# Revit family: IS_Mara_A9041_BIM_IT
name_source: partatom
category: Plumbing Fixtures
revit_build: Autodesk Revit MEP 2016 (Build: 20161004_0715(x64)
units: mm (PartAtom-declared; Revit-internal decimal feet)

## family parameters
Always vertical = No
Cut with Voids When Loaded = No
OmniClass Number = 23.45.55.17
OmniClass Title = Mixing Faucets
Part Type = Normal
Room Calculation Point = No
Round Connector Dimension = Use Diameter
Shared = No
Work Plane-Based = No

## types (1)
- A9041AA - MARA MISC LVB C/LIM PORTATA BOCCA 120 CR
    Accessori = www.idealstandard.it
    AltezzaNominale = 169 mm  [stored 0.554462 ft]
    Assembly Code = C1030200
    Autore = Ideal Standard Italia
    BIMobject category = Taps & Mixers
    BOSUseNativeGeometries = 1
    Brand = Ideal Standard
    Brand url = http://www.idealstandard.co.uk
    Caratteristiche = Miscelatore monocomando lavabo, con bocca di erogazione fissa da 120 mm. È dotato di cartuccia da 35 mm con limitatore della temperatura e riduttore di portata a 5 l/min. Sistema di fissaggio Easy Fix. Sporgenza bocca 120 mm, altezza bocca 65 mm. Con asta di comando e piletta in metallo cromato da 1-1/4”. Tubi flessibili.
    CodiceABarre = 3800861033394
    Colore = Cromato
    Connessione = Installazione
    CostoDiSostituzione = 0 $
    Description = MARA - Miscelatore monocomando lavabo, con bocca di erogazione fissa da 120 mm. È dotato di cartuccia da 35 mm con limitatore della temperatura e riduttore di portata a 5 l/min. Sistema di fissaggio Easy Fix. Sporgenza bocca 120 mm, altezza bocca 65 mm. Con asta di comando e piletta in metallo cromato da 1-1/4”. Tubi flessibili.
    DescrizioneClassifcazioneUni2015 = Washbasin taps ?
    Dimensione = 169 x 50 x 157
    DurataGaranziaProdotti = 5
    EAN code = https://3800861033394
    Edition number = 1
    Finitura = Cromato
    Garanzia = Garanzia Idealstandard
    IFC Classification = Sanitary Terminal
    InformazioniDiProdotto = www.idealstandard.it/prodotti/html
    InformazioniGaranzia = www.idealstandard.it/garanzia.html
    Installation instructions = www.idealstandard.it/prodotti/html
    InstruzioniInstallazione = www.idealstandard.it/prodotti/html
    LarghezzaNominale = 50 mm  [stored 0.164042 ft]
    LunghezzaNominale = 157 mm
    Manufacturer = www.idealstandard.it
    Manufacturer name = Ideal Standard
    Material main = Brass
    Materiale = Ottone
    Model = A9041AA
    NBS Reference Code = 35-79-95
    NBS Reference Description = Wash Basin And Trough Water Supply Fittings
    Nominal height = 169
    Nominal width = 50
    NumeroDiModello = A9041AA
    OmniClass Code = 23-31 11 00
    OmniClass Description = Faucets
    PesoNetto = 1,418 KG
    Product Guid = fabe5e2e-1783-4b92-abe1-92f1cb9e871c
    Product SKU = A9041
    Product certification = http://www.idealstandard.it
    Product data url = https://bimobject.com
    Product family = MARA
    Product group = Basin Mixer
    Product name = MARA BASIN MIXER RIM GRANDE 5L/MIN PU/M. SPX
    Product url = http://www.idealstandard.it
    QR code = http://bimobject.com
    Revisione = 1
    RiferimentoClassificazioneUni2015 = Pr_40_20_87_98
    Spazio = Interno
    Technical description = www.idealstandard.it/prodotti/html
    Telefono = 800 652 290
    URL = www.idealstandard.it
    Uniclass 1.4 Code = L8212
    Uniclass 1.4 Description = Fittings
    Uniclass 2.0 Code = PR-35-79-95
    Uniclass 2.0 Description = Wash Basin And Trough Water Supply Fittings
    Uniclass 2015 Code = Pr_40_20_87_96
    Uniclass 2015 Name = Washbasin manual water supply sets
    UnitaDurata = anni
    UnitaDurataGaranzia = anni
    UnitaLineare = milimetri
    UnitaVolume = Litri
    Versione = 1
    VersioneClassificazioneUni2015 = Products v1.1
    Weight Net (Kg) = 1.42

note: [stored X ft] marks values corroborated as IEEE doubles in the binary element streams (Revit-internal decimal feet)

## geometry (parser evidence)
native form markers: Blend x4
no freeform markers — native parametric forms only
